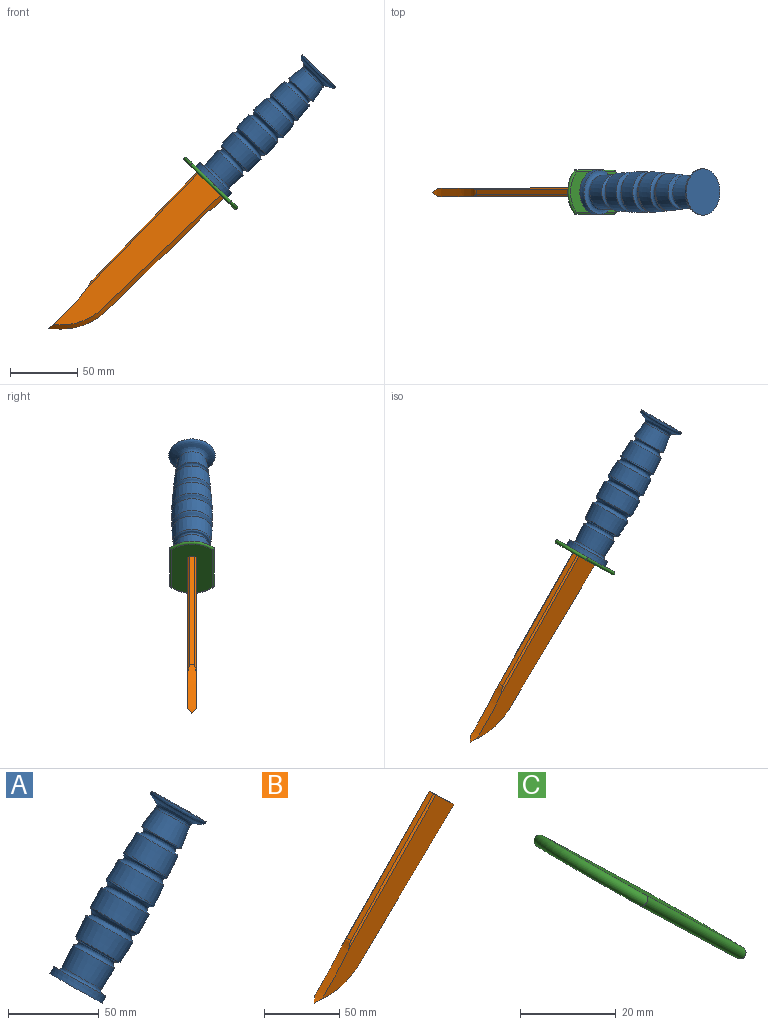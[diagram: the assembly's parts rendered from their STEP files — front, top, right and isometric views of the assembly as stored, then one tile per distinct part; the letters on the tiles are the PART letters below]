
ASSEMBLY  parts=3 mates=2
PART A: 16 faces, bbox 104.1x34.5x106 mm
  f0: plane 33.02x23.74mm, normal (-0.69,0,-0.72), area 856.3mm2, adj f1
  f1: cone r=16.39mm half-angle=1.6deg, axis (-0.69,0,-0.72), area 446.3mm2, adj f0,f2
  f2: revolved ~32.79x23.57mm, area 467mm2, adj f1,f3
  f3: cone r=13.14mm half-angle=2.9deg, axis (0.69,0,0.72), area 1082.5mm2, adj f2,f4
  f4: revolved ~28.25x22.83mm, area 557.7mm2, adj f3,f5
  f5: cone r=14.88mm half-angle=3.4deg, axis (0.69,0,0.72), area 1157.5mm2, adj f4,f6
  f6: revolved ~30.28x25.53mm, area 674.1mm2, adj f5,f7
  f7: cone r=15.08mm half-angle=0.3deg, axis (-0.69,0,-0.72), area 1157.6mm2, adj f6,f8
  f8: revolved ~30.17x25.74mm, area 713mm2, adj f7,f9
  f9: cone r=14.34mm half-angle=3.1deg, axis (-0.69,0,-0.72), area 1100.3mm2, adj f8,f10
  f10: revolved ~28.69x23.87mm, area 553.5mm2, adj f9,f11
  f11: cone r=13.07mm half-angle=3.3deg, axis (-0.69,0,-0.72), area 1072.6mm2, adj f10,f12
  f12: revolved ~26.15x21.57mm, area 538.8mm2, adj f11,f13
  f13: cone r=10.66mm half-angle=8.5deg, axis (-0.69,0,-0.72), area 926.1mm2, adj f12,f14
  f14: revolved ~34.54x25.73mm, area 919.8mm2, adj f13,f15
  f15: plane 34.54x24.84mm, normal (0.69,0,0.72), area 937.2mm2, adj f14
PART B: 11 faces, bbox 141.3x8.8x121.6 mm
  f0: extruded ~2.22x2.16mm, area 2.6mm2, adj f4,f6,f9
  f1: plane 20x19.33mm, normal (0.69,0,0.72), area 165mm2, adj f2,f5,f6,f7,f8,f9,f10
  f2: plane 80.36x77.67mm, normal (-0.72,0,0.69), area 425.8mm2, adj f1,f3,f7,f10
  f3: extruded ~35.66x32.66mm, area 288.7mm2, adj f2,f5,f6,f7,f8,f9,f10
  f4: plane 19.75x19.09mm, normal (0.72,0,-0.69), area 29.6mm2, adj f0,f6,f9
  f5: plane 124.22x112.63mm, normal (0,-1,0), area 3004.6mm2, adj f1,f3,f6,f7
  f6: bspline ~138.77x107.61mm, area 714.1mm2, adj f0,f1,f3,f4,f5,f9
  f7: plane 88.32x84.6mm, normal (-0.51,-0.71,0.49), area 207mm2, adj f1,f2,f3,f5
  f8: plane 124.22x112.63mm, normal (0,1,0), area 3063.6mm2, adj f1,f3,f9,f10
  f9: bspline ~138.77x107.61mm, area 714.1mm2, adj f0,f1,f3,f4,f6,f8
  f10: plane 88.32x84.6mm, normal (-0.51,0.71,0.49), area 207mm2, adj f1,f2,f3,f8
PART C: 6 faces, bbox 42.1x35.7x40.7 mm
  f0: plane 37.53x36.28mm, normal (-0.69,0,-0.72), area 1471.6mm2, adj f2,f3,f4,f5
  f1: plane 37.53x36.28mm, normal (0.69,0,0.72), area 1471.6mm2, adj f2,f3,f4,f5
  f2: torus R=21.59mm, axis (-0.69,0,-0.72), area 142.8mm2, adj f0,f1,f3,f4
  f3: cylinder r=1.27mm len=30.99mm, axis (-0.72,0,0.69), area 160.7mm2, adj f0,f1,f2,f5
  f4: cylinder r=1.27mm len=30.99mm, axis (0.72,0,-0.69), area 160.7mm2, adj f0,f1,f2,f5
  f5: torus R=21.59mm, axis (-0.69,0,-0.72), area 142.8mm2, adj f0,f1,f3,f4
PLACE A t=(-67.13,119.87,-61.84)mm
PLACE B t=(-66.84,119.87,-62.02)mm
PLACE C t=(-67.13,119.87,-61.84)mm
MATE fastened C.f1 <-> A.f13  axis (0.69,0,0.72) through (56.21,119.87,54.8)mm
MATE fastened C.f0 <-> B.f1  axis (-0.69,0,-0.72) through (54.45,119.87,52.98)mm
